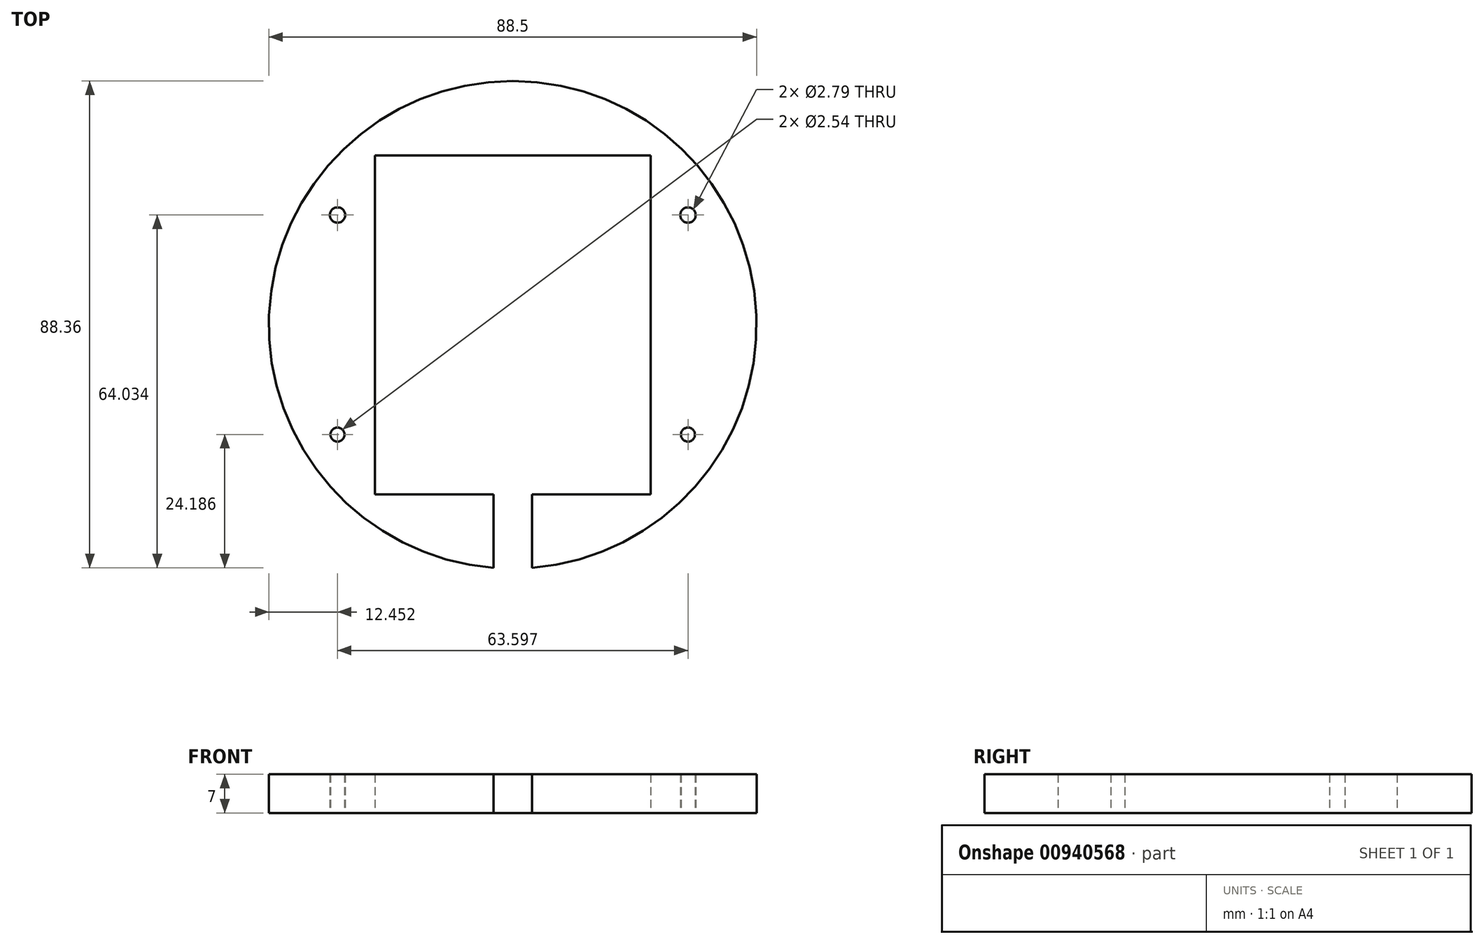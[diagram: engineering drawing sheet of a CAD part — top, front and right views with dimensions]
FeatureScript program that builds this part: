
annotation { "Feature Type Name" : "Feature", "Feature Type Description" : "" }
export const myFeature = defineFeature(function(context is Context, id is Id, definition is map)
    precondition{}
    {
        {
            var Q0;
            Q0=qCreatedBy(makeId("Top.planeOp"),FACE);
            var sketch = newSketch(context, id + "F0", { "sketchPlane" : qUnion([Q0])});
            skCircle(sketch, "E0", {"center": v(0, 0) * mm, "radius": 44.25 * mm});
            skLineSegment(sketch, "E1.bottom", {"start": v(25.02, -30.77) * mm, "end": v(3.5, -30.77) * mm});
            skLineSegment(sketch, "E1.top", {"start": v(25.02, 30.77) * mm, "end": v(-25.02, 30.77) * mm});
            skLineSegment(sketch, "E1.left", {"start": v(25.02, -30.77) * mm, "end": v(25.02, 30.77) * mm});
            skLineSegment(sketch, "E1.right", {"start": v(-25.02, -30.77) * mm, "end": v(-25.02, 30.77) * mm});
            skLineSegment(sketch, "E2.left", {"start": v(3.5, -30.77) * mm, "end": v(3.5, -44.11) * mm});
            skLineSegment(sketch, "E2.right", {"start": v(-3.5, -30.77) * mm, "end": v(-3.5, -44.11) * mm});
            skPoint(sketch, "E2.middle", {"position": v(0, -44.25) * mm});
            skPoint(sketch, "E2.middle.positionSnap0", {"position": v(0, -30.77) * mm});
            skPoint(sketch, "E2.centerSnap0", {"position": v(0, -30.77) * mm});
            skPoint(sketch, "E2.top.end.orphan", {"position": v(-3.5, -57.73) * mm});
            skPoint(sketch, "E2.top.start.orphan", {"position": v(3.5, -57.73) * mm});
            skLineSegment(sketch, "E3.trimOffspring", {"start": v(-3.5, -30.77) * mm, "end": v(-25.02, -30.77) * mm});
            skLineSegment(sketch, "E4", {"start": v(-25.02, 30.77) * mm, "end": v(-44.25, 0) * mm, "construction": true});
            skPoint(sketch, "E4.endSnap0", {"position": v(-25.02, 0) * mm});
            skLineSegment(sketch, "E5", {"start": v(-44.25, 0) * mm, "end": v(-25.02, -30.77) * mm, "construction": true});
            skLineSegment(sketch, "E6", {"start": v(-25.02, 30.77) * mm, "end": v(-31.8, 30.77) * mm, "construction": true});
            skLineSegment(sketch, "E7", {"start": v(-31.8, 30.77) * mm, "end": v(-31.8, -30.77) * mm, "construction": true});
            skLineSegment(sketch, "E8", {"start": v(-31.8, -30.77) * mm, "end": v(-25.02, -30.77) * mm, "construction": true});
            skPoint(sketch, "E9", {"position": v(-31.8, -19.92) * mm});
            skPoint(sketch, "E10", {"position": v(-31.8, 19.92) * mm});
            skCircle(sketch, "E11", {"center": v(-31.8, -19.92) * mm, "radius": 1.27 * mm});
            skCircle(sketch, "E12", {"center": v(-31.8, 19.92) * mm, "radius": 1.4 * mm});
            skLineSegment(sketch, "E13", {"start": v(0, -68.48) * mm, "end": v(0, 54.35) * mm, "construction": true});
            skLineSegment(sketch, "E14", {"start": v(-55.34, 0) * mm, "end": v(69.3, 0) * mm, "construction": true});
            skCircle(sketch, "E15.MirrorC", {"center": v(31.8, 19.92) * mm, "radius": 1.4 * mm});
            skCircle(sketch, "E16.MirrorC", {"center": v(31.8, -19.92) * mm, "radius": 1.27 * mm});
            skSolve(sketch);
        }
        {
            var Q0;
            Q0=makeQuery(id+"F0.imprint","IMPRINT",FACE,{"disambiguationData":[TD([[makeQuery(id+"F0.imprint","IMPRINT",EDGE,{"derivedFrom":sQuery(id+"F0.wireOp",EDGE,"E1.bottom")}),1.0]])]});
            extrude(context, id + "F1", {"entities" : qUnion([Q0]), "depth" : 7 * mm, "offsetDistance" : 25.4 * mm});
        }
    });
